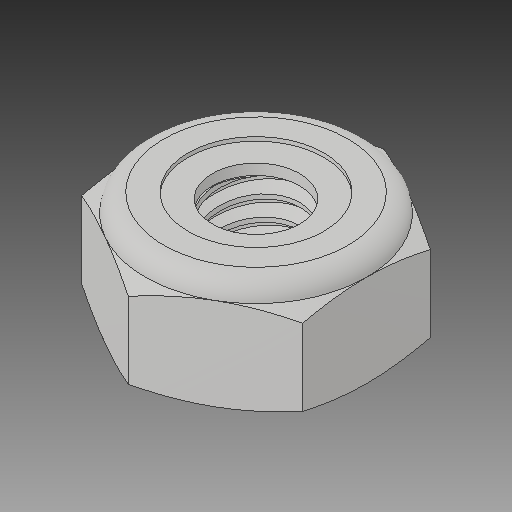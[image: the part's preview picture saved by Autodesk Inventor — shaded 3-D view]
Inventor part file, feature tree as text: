
AUTODESK INVENTOR PART (.ipt)
format: ipt  version: 2018 (Build 220112000, 112)  size: 275,456 bytes
history: native  units: in
note: dims shown in document units (in); Inventor stores cm internally (conversion verified against a paired STEP export)
features: other x1, revolve x1
ambient origin geometry x8: Origin, YZ Plane, XZ Plane, XY Plane, X Axis, Y Axis, Z Axis, Center Point
bodies: Solid1 (feature_tree), Solid2 (feature_tree)
feature tree (2):
  other  "Cut-Revolve4"
  revolve  "Revolve2"  [1 undecoded]
note: 1 required parameter value undecoded (feature->parameter linkage not recoverable at this tier; creation-order binding heuristic only, values carry confidence <= 0.55)
